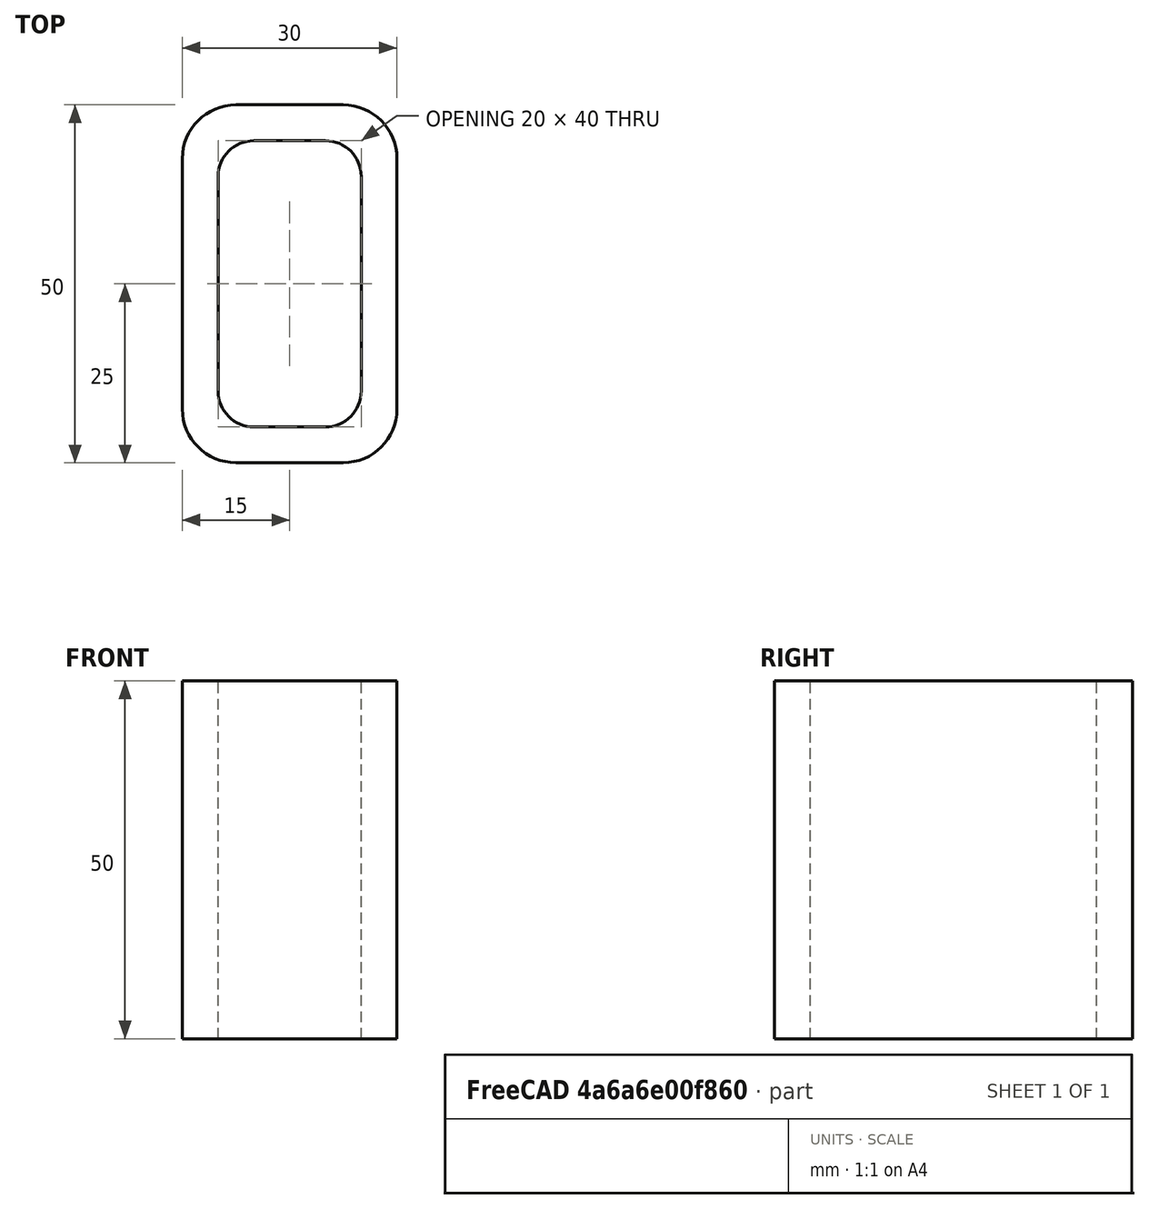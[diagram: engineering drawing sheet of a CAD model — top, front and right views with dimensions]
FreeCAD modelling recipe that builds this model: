
FCSTD DOCUMENT  (FreeCAD 0.15R4671 (Git))
Label: Rectangular hollow section 50x30x5 EN10219 S235JRH
License: All rights reserved
LicenseURL: http://en.wikipedia.org/wiki/All_rights_reserved
objects: Sketcher::SketchObject×1, Part::Extrusion×1
note: 2 computed .brp shape members not serialized (recipe doc carries the construction recipe); baked Part::Feature solids carry a one-line shape summary decoded from their .brp

FEATURE [Sketcher::SketchObject] Sketch
  sketch-geometry (16):
    g0: LineSegment StartX=-5 StartY=20 StartZ=0 EndX=5 EndY=20 EndZ=0
    g1: LineSegment StartX=10 StartY=15 StartZ=0 EndX=10 EndY=-15 EndZ=0
    g2: LineSegment StartX=5 StartY=-20 StartZ=0 EndX=-5 EndY=-20 EndZ=0
    g3: LineSegment StartX=-10 StartY=-15 StartZ=0 EndX=-10 EndY=15 EndZ=0
    g4: LineSegment StartX=-7.5 StartY=25 StartZ=0 EndX=7.5 EndY=25 EndZ=0
    g5: LineSegment StartX=15 StartY=17.5 StartZ=0 EndX=15 EndY=-17.5 EndZ=0
    g6: LineSegment StartX=7.5 StartY=-25 StartZ=0 EndX=-7.5 EndY=-25 EndZ=0
    g7: LineSegment StartX=-15 StartY=-17.5 StartZ=0 EndX=-15 EndY=17.5 EndZ=0
    g8: ArcOfCircle CenterX=-5 CenterY=15 CenterZ=0 NormalX=0 NormalY=0 NormalZ=1 Radius=5 StartAngle=1.5708 EndAngle=3.14159
    g9: ArcOfCircle CenterX=5 CenterY=15 CenterZ=0 NormalX=0 NormalY=0 NormalZ=1 Radius=5 StartAngle=0 EndAngle=1.5708
    g10: ArcOfCircle CenterX=5 CenterY=-15 CenterZ=0 NormalX=0 NormalY=0 NormalZ=1 Radius=5 StartAngle=4.71239 EndAngle=6.28319
    g11: ArcOfCircle CenterX=-5 CenterY=-15 CenterZ=0 NormalX=0 NormalY=0 NormalZ=1 Radius=5 StartAngle=3.14159 EndAngle=4.71239
    g12: ArcOfCircle CenterX=7.5 CenterY=17.5 CenterZ=0 NormalX=0 NormalY=0 NormalZ=1 Radius=7.5 StartAngle=0 EndAngle=1.5708
    g13: ArcOfCircle CenterX=7.5 CenterY=-17.5 CenterZ=0 NormalX=0 NormalY=0 NormalZ=1 Radius=7.5 StartAngle=4.71239 EndAngle=6.28319
    g14: ArcOfCircle CenterX=-7.5 CenterY=-17.5 CenterZ=0 NormalX=0 NormalY=0 NormalZ=1 Radius=7.5 StartAngle=3.14159 EndAngle=4.71239
    g15: ArcOfCircle CenterX=-7.5 CenterY=17.5 CenterZ=0 NormalX=0 NormalY=0 NormalZ=1 Radius=7.5 StartAngle=1.5708 EndAngle=3.14159
  constraints (36):
    c: Horizontal(g2)
    c: Vertical(g3)
    c: Horizontal(g6)
    c: Vertical(g7)
    c: Tangent(g3,g8) = 1.5708
    c: Tangent(g0,g8) = 1.5708
    c: Tangent(g0,g9) = 1.5708
    c: Tangent(g1,g9) = 1.5708
    c: Tangent(g1,g10) = 1.5708
    c: Tangent(g2,g10) = 1.5708
    c: Tangent(g2,g11) = 1.5708
    c: Tangent(g3,g11) = 1.5708
    c: Tangent(g4,g12) = 1.5708
    c: Tangent(g5,g12) = 1.5708
    c: Tangent(g5,g13) = 1.5708
    c: Tangent(g6,g13) = 1.5708
    c: Tangent(g6,g14) = 1.5708
    c: Tangent(g7,g14) = 1.5708
    c: Tangent(g7,g15) = 1.5708
    c: Tangent(g4,g15) = 1.5708
    c: Equal(g9,g8)
    c: Equal(g9,g11)
    c: Equal(g9,g10)
    c: Equal(g12,g15)
    c: Equal(g12,g14)
    c: Equal(g12,g13)
    c: Symmetric(g4,g6,g-1)
    c: Symmetric(g7,g5,g-2)
    c: DistanceY(g4,g6) = -50
    c: DistanceX(g7,g5) = 30
    c: Symmetric(g3,g1,g-2)
    c: Symmetric(g0,g2,g-1)
    c: DistanceY(g0,g4) = 5
    c: DistanceX(g5,g1) = -5
    c: Radius(g9) = 5
    c: Radius(g12) = 7.5
FEATURE [Part::Extrusion] Extrude  label="Rectangular hollow section 50x30x5 EN10219 S235JRH"
  Base = -> Sketch
  Dir = (0,0,50)
  Solid = true
